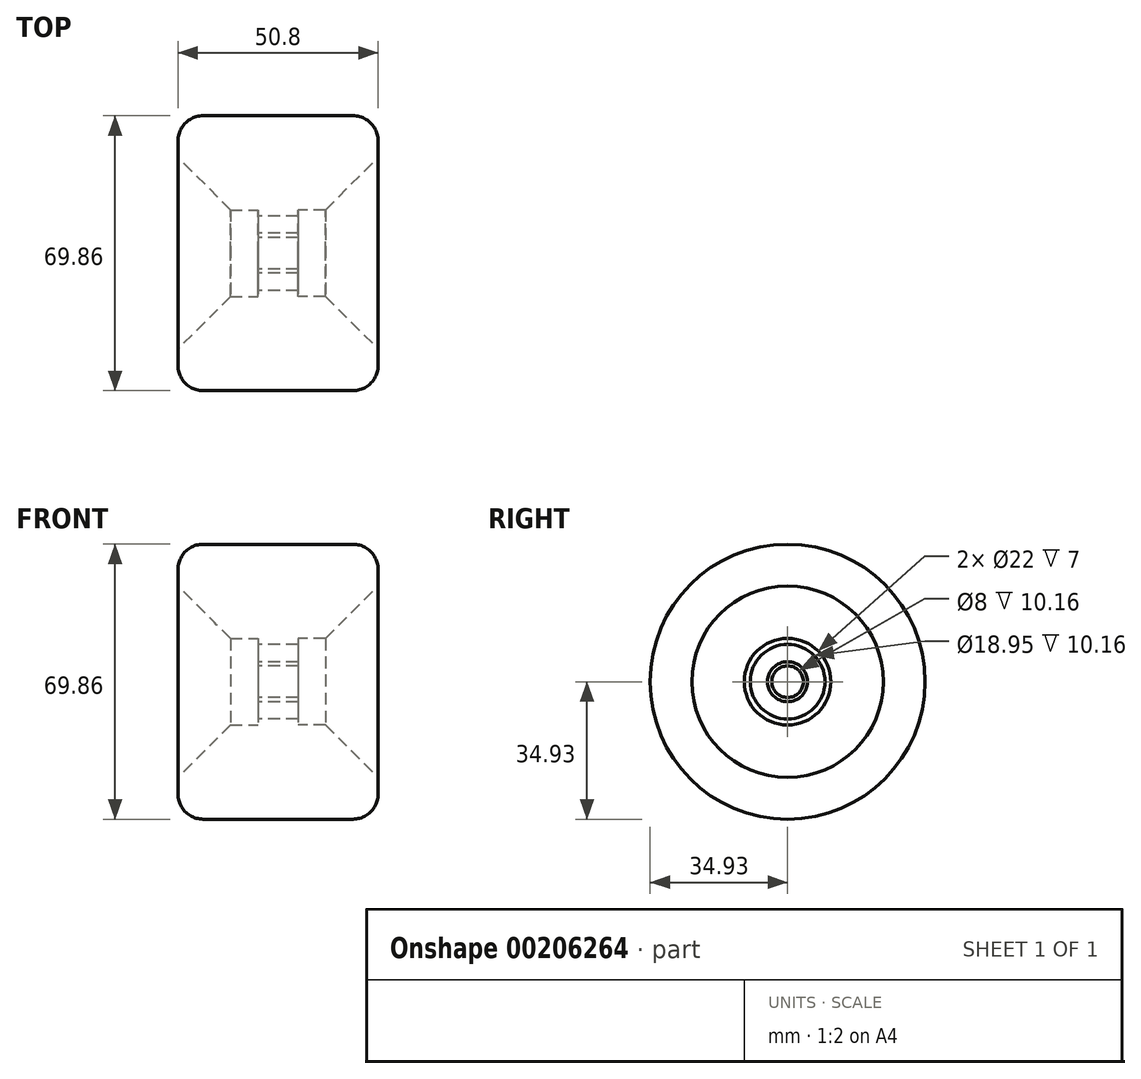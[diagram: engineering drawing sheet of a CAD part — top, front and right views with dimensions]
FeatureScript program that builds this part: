
annotation { "Feature Type Name" : "Feature", "Feature Type Description" : "" }
export const myFeature = defineFeature(function(context is Context, id is Id, definition is map)
    precondition{}
    {
        {
            var Q0;
            Q0=qCreatedBy(makeId("Front.planeOp"),FACE);
            var sketch = newSketch(context, id + "F0", { "sketchPlane" : qUnion([Q0])});
            skLineSegment(sketch, "E0", {"start": v(0, 34.93) * mm, "end": v(19.05, 34.93) * mm});
            skArc(sketch, "E1", {"start": v(19.05, 34.93) * mm, "mid": v(23.54, 33.07) * mm, "end": v(25.4, 28.58) * mm});
            skLineSegment(sketch, "E2", {"start": v(25.4, 28.58) * mm, "end": v(25.4, 24.32) * mm});
            skLineSegment(sketch, "E3", {"start": v(25.4, 24.32) * mm, "end": v(12.08, 11) * mm});
            skLineSegment(sketch, "E4", {"start": v(12.08, 11) * mm, "end": v(5.08, 11) * mm});
            skLineSegment(sketch, "E5", {"start": v(5.08, 11) * mm, "end": v(5.08, 9.48) * mm});
            skLineSegment(sketch, "E6", {"start": v(5.08, 9.48) * mm, "end": v(0, 9.48) * mm});
            skLineSegment(sketch, "E7", {"start": v(0, 9.48) * mm, "end": v(0, 34.93) * mm});
            skLineSegment(sketch, "E8", {"start": v(0, 0) * mm, "end": v(18.8, 0) * mm, "construction": true});
            skSolve(sketch);
        }
        {
            var Q0;
            Q0=qSketchRegion(id+"F0",true);
            var Q1;
            Q1=sQuery(id+"F0.wireOp",EDGE,"E8");
            revolve(context, id + "F1", {"entities" : qUnion([Q0]), "axis" : qUnion([Q1]), "revolveType" : RevolveType.FULL});
        }
        {
            var Q0;
            Q0=makeQuery(id+"F1.opRevolve","SWEPT_BODY",BODY,{"disambiguationData":[OSD([sQuery(id+"F0.wireOp",EDGE,"E0"),sQuery(id+"F0.wireOp",EDGE,"E1"),sQuery(id+"F0.wireOp",EDGE,"E2"),sQuery(id+"F0.wireOp",EDGE,"E3"),sQuery(id+"F0.wireOp",EDGE,"E4"),sQuery(id+"F0.wireOp",EDGE,"E5"),sQuery(id+"F0.wireOp",EDGE,"E6"),sQuery(id+"F0.wireOp",EDGE,"E7")])]});
            var Q1;
            Q1=makeQuery(id+"F1.opRevolve","SWEPT_FACE",FACE,{"disambiguationData":[OSD([sQuery(id+"F0.wireOp",EDGE,"E7")])]});
            mirror(context, id + "F2", {"operationType" : NewBodyOperationType.ADD, "entities" : qUnion([Q0]), "mirrorPlane" : qUnion([Q1])});
        }
        {
            var Q0;
            Q0=qCreatedBy(makeId("Front.planeOp"),FACE);
            var sketch = newSketch(context, id + "F3", { "sketchPlane" : qUnion([Q0])});
            skLineSegment(sketch, "E9.bottom", {"start": v(-5.08, 5.08) * mm, "end": v(5.08, 5.08) * mm});
            skLineSegment(sketch, "E9.top", {"start": v(-5.08, 4) * mm, "end": v(5.08, 4) * mm});
            skLineSegment(sketch, "E9.left", {"start": v(-5.08, 5.08) * mm, "end": v(-5.08, 4) * mm});
            skLineSegment(sketch, "E9.right", {"start": v(5.08, 5.08) * mm, "end": v(5.08, 4) * mm});
            skLineSegment(sketch, "E10", {"start": v(0, 0) * mm, "end": v(5.4, 0) * mm, "construction": true});
            skSolve(sketch);
        }
        {
            var Q0;
            Q0=qSketchRegion(id+"F3",true);
            var Q1;
            Q1=sQuery(id+"F3.wireOp",EDGE,"E10");
            revolve(context, id + "F4", {"entities" : qUnion([Q0]), "axis" : qUnion([Q1]), "revolveType" : RevolveType.FULL});
        }
    });
